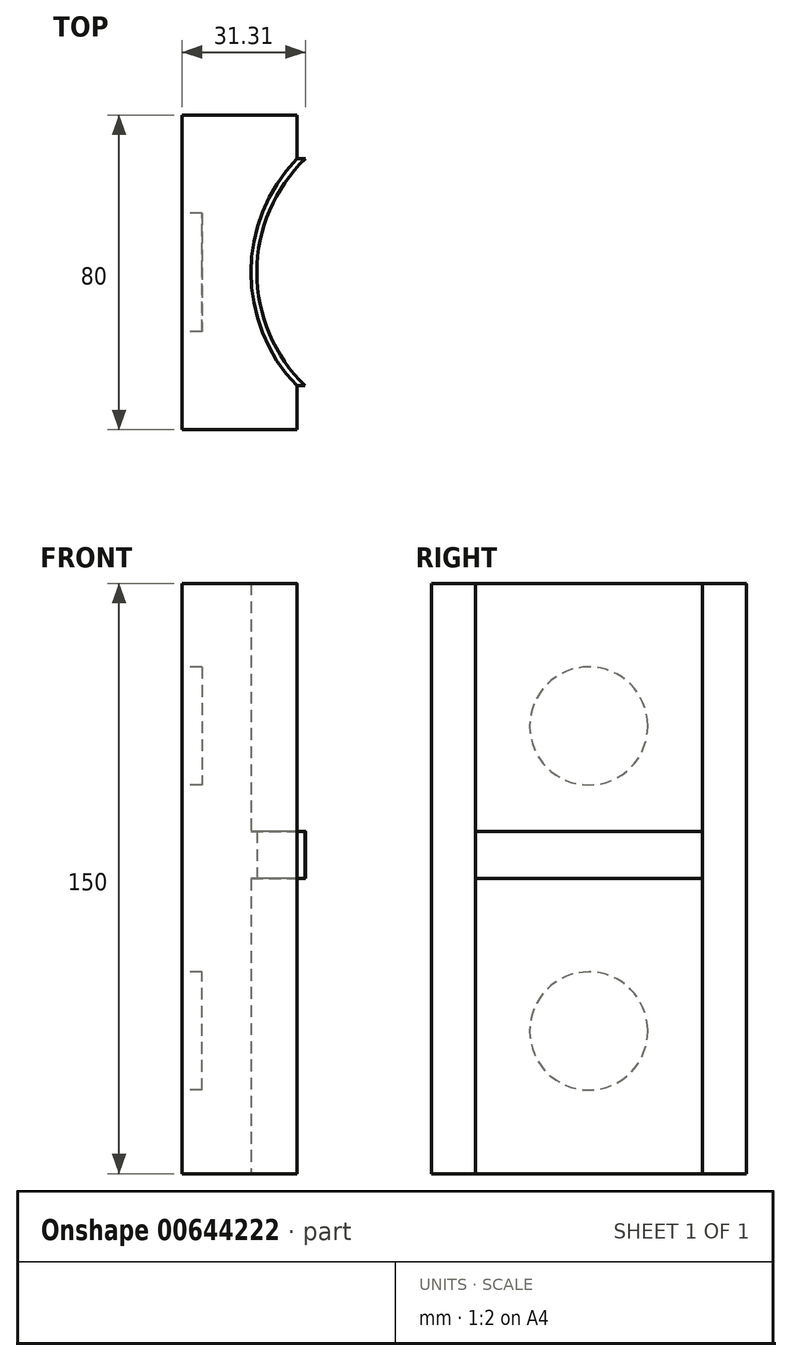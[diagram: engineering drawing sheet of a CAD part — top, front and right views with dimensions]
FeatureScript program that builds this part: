
annotation { "Feature Type Name" : "Feature", "Feature Type Description" : "" }
export const myFeature = defineFeature(function(context is Context, id is Id, definition is map)
    precondition{}
    {
        {
            var Q0;
            Q0=qCreatedBy(makeId("Top.planeOp"),FACE);
            var sketch = newSketch(context, id + "F0", { "sketchPlane" : qUnion([Q0])});
            skLineSegment(sketch, "E0.left", {"start": v(-59, 40) * mm, "end": v(-59, -40) * mm});
            skPoint(sketch, "E1", {"position": v(-41.5, 0) * mm});
            skArc(sketch, "E2", {"start": v(-41.5, 0) * mm, "mid": v(-38.47, 15.57) * mm, "end": v(-29.81, 28.87) * mm});
            skPoint(sketch, "E3", {"position": v(0, -41) * mm});
            skArc(sketch, "E4", {"start": v(-41.5, 0) * mm, "mid": v(-38.48, -15.54) * mm, "end": v(-29.86, -28.82) * mm});
            skLineSegment(sketch, "E5", {"start": v(-29.8, 40) * mm, "end": v(-29.87, -40) * mm});
            skLineSegment(sketch, "E6", {"start": v(-29.86, -28.82) * mm, "end": v(-29.86, -28.82) * mm});
            skLineSegment(sketch, "E7", {"start": v(-59, -40) * mm, "end": v(-29.87, -40) * mm});
            skLineSegment(sketch, "E8", {"start": v(-59, 40) * mm, "end": v(-29.8, 40) * mm});
            skCircle(sketch, "E9", {"center": v(0, 0) * mm, "radius": 40 * mm});
            skLineSegment(sketch, "E10", {"start": v(-29.81, 28.87) * mm, "end": v(-27.69, 28.87) * mm});
            skLineSegment(sketch, "E11", {"start": v(-29.86, -28.82) * mm, "end": v(-27.74, -28.82) * mm});
            skSolve(sketch);
        }
        {
            var Q0;
            {var subQ0=sQuery(id+"F0.wireOp",EDGE,"E9");var subQ1=sQuery(id+"F0.wireOp",EDGE,"E5");var subQ2=makeQuery(id+"F0.imprint","INTERSECT",VERTEX,{"disambiguationData":[OD(0.0)],"derivedFrom":[subQ1,subQ0]});Q0=makeQuery(id+"F0.imprint","IMPRINT",FACE,{"disambiguationData":[TD([[makeQuery(id+"F0.imprint","IMPRINT",EDGE,{"disambiguationData":[TD([[subQ2,-1.0]])],"derivedFrom":subQ1}),1.0]])]});}
            var Q1;
            {var subQ0=sQuery(id+"F0.wireOp",EDGE,"E10");Q1=makeQuery(id+"F0.imprint","IMPRINT",FACE,{"disambiguationData":[TD([[makeQuery(id+"F0.imprint","IMPRINT",EDGE,{"derivedFrom":subQ0}),-1.0]])]});}
            var Q2;
            {var subQ1=sQuery(id+"F0.wireOp",EDGE,"E2");Q2=makeQuery(id+"F0.imprint","IMPRINT",FACE,{"disambiguationData":[TD([[makeQuery(id+"F0.imprint","IMPRINT",EDGE,{"derivedFrom":subQ1}),-1.0]])]});}
            var Q3;
            {var subQ0=sQuery(id+"F0.wireOp",EDGE,"E9");var subQ1=sQuery(id+"F0.wireOp",EDGE,"E5");var subQ2=makeQuery(id+"F0.imprint","INTERSECT",VERTEX,{"disambiguationData":[OD(0.0)],"derivedFrom":[subQ1,subQ0]});Q3=makeQuery(id+"F0.imprint","IMPRINT",FACE,{"disambiguationData":[TD([[makeQuery(id+"F0.imprint","IMPRINT",EDGE,{"disambiguationData":[TD([[subQ2,-1.0]])],"derivedFrom":subQ1}),-1.0]])]});}
            var Q4;
            {var subQ0=sQuery(id+"F0.wireOp",EDGE,"E11");Q4=makeQuery(id+"F0.imprint","IMPRINT",FACE,{"disambiguationData":[TD([[makeQuery(id+"F0.imprint","IMPRINT",EDGE,{"derivedFrom":subQ0}),1.0]])]});}
            extrude(context, id + "F1", {"entities" : qUnion([Q0, Q1, Q2, Q3, Q4]), "depth" : 12 * mm, "offsetDistance" : 25 * mm});
        }
        {
            var Q0;
            {var subQ1=sQuery(id+"F0.wireOp",EDGE,"E0.left");Q0=makeQuery(id+"F0.imprint","IMPRINT",FACE,{"disambiguationData":[TD([[makeQuery(id+"F0.imprint","IMPRINT",EDGE,{"derivedFrom":subQ1}),1.0]])]});}
            extrude(context, id + "F2", {"entities" : qUnion([Q0]), "depth" : 75 * mm, "offsetDistance" : 25 * mm});
        }
        {
            var Q0;
            Q0=makeQuery(id+"F1.opExtrude","CAP_FACE",FACE,{"disambiguationData":[OSD([sQuery(id+"F0.wireOp",EDGE,"E2"),sQuery(id+"F0.wireOp",EDGE,"E4"),sQuery(id+"F0.wireOp",EDGE,"E9"),sQuery(id+"F0.wireOp",EDGE,"E10"),sQuery(id+"F0.wireOp",EDGE,"E11")])],"isStart":false});
            var sketch = newSketch(context, id + "F3", { "sketchPlane" : qUnion([Q0])});
            skCircle(sketch, "E12", {"center": v(0, 0) * mm, "radius": 7 * mm});
            skSolve(sketch);
        }
        {
            var Q0;
            Q0=makeQuery(id+"F3.imprint","IMPRINT",FACE,{"disambiguationData":[TD([[makeQuery(id+"F3.imprint","IMPRINT",EDGE,{"derivedFrom":sQuery(id+"F3.wireOp",EDGE,"E12")}),1.0]])]});
            var Q1;
            Q1=sQuery(id+"F3.wireOp",EDGE,"E12");
            extrude(context, id + "F4", {"entities" : qUnion([Q0]), "operationType" : NewBodyOperationType.REMOVE, "surfaceEntities" : qUnion([Q1]), "oppositeDirection" : true, "depth" : 25 * mm, "offsetDistance" : 25 * mm});
        }
        {
            var Q0;
            Q0=makeQuery(id+"F2.opExtrude","SWEPT_FACE",FACE,{"disambiguationData":[OSD([sQuery(id+"F0.wireOp",EDGE,"E0.left")])]});
            var sketch = newSketch(context, id + "F5", { "sketchPlane" : qUnion([Q0])});
            skCircle(sketch, "E13", {"center": v(0, 38.75) * mm, "radius": 15 * mm});
            skSolve(sketch);
        }
        {
            var Q0;
            Q0=makeQuery(id+"F5.imprint","IMPRINT",FACE,{"disambiguationData":[TD([[makeQuery(id+"F5.imprint","IMPRINT",EDGE,{"derivedFrom":sQuery(id+"F5.wireOp",EDGE,"E13")}),1.0]])]});
            extrude(context, id + "F6", {"entities" : qUnion([Q0]), "operationType" : NewBodyOperationType.REMOVE, "oppositeDirection" : true, "depth" : 5 * mm, "offsetDistance" : 25 * mm});
        }
        {
            var Q0;
            Q0=makeQuery(id+"F2.opExtrude","SWEPT_BODY",BODY,{"disambiguationData":[OSD([sQuery(id+"F0.wireOp",EDGE,"E0.left"),sQuery(id+"F0.wireOp",EDGE,"E2"),sQuery(id+"F0.wireOp",EDGE,"E4"),sQuery(id+"F0.wireOp",EDGE,"E5"),sQuery(id+"F0.wireOp",EDGE,"E7"),sQuery(id+"F0.wireOp",EDGE,"E8")])]});
            var Q1;
            Q1=qCreatedBy(makeId("Top.planeOp"),FACE);
            mirror(context, id + "F7", {"operationType" : NewBodyOperationType.ADD, "entities" : qUnion([Q0]), "mirrorPlane" : qUnion([Q1])});
        }
    });
